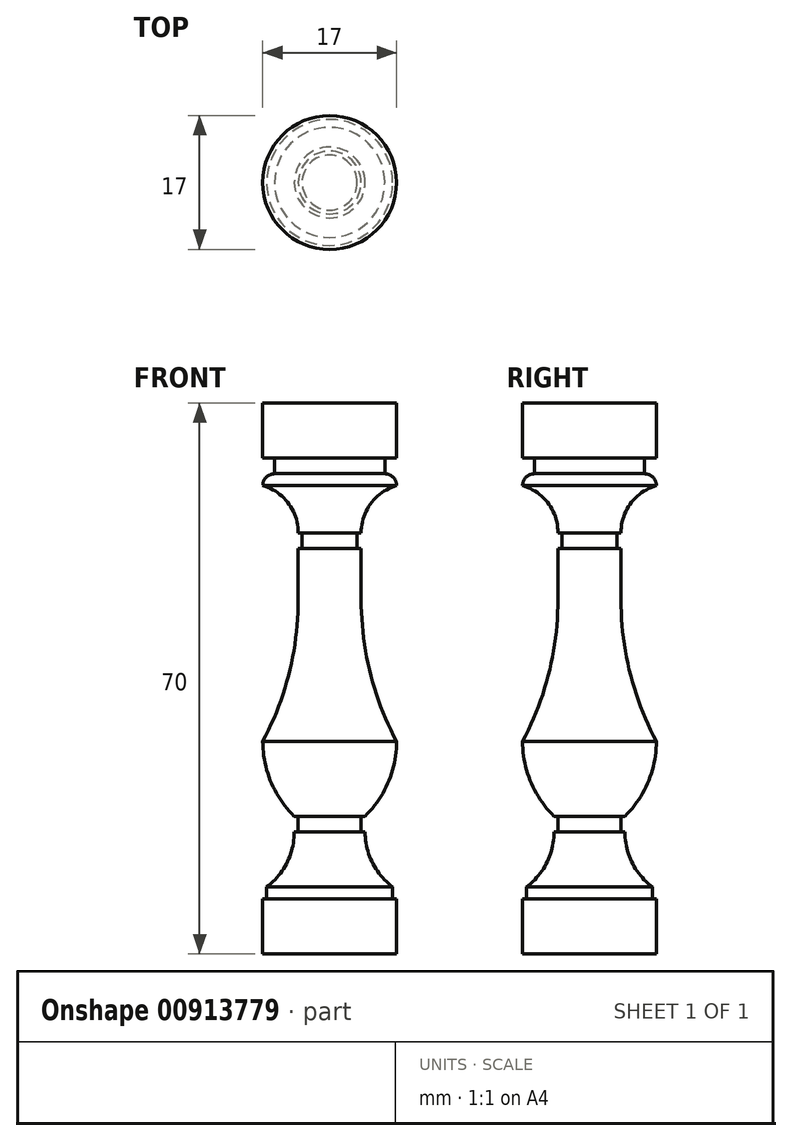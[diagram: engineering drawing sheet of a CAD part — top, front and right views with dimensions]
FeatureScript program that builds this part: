
annotation { "Feature Type Name" : "Feature", "Feature Type Description" : "" }
export const myFeature = defineFeature(function(context is Context, id is Id, definition is map)
    precondition{}
    {
        {
            var Q0;
            Q0=qCreatedBy(makeId("Front.planeOp"),FACE);
            var sketch = newSketch(context, id + "F0", { "sketchPlane" : qUnion([Q0])});
            skLineSegment(sketch, "E0", {"start": v(0, 0) * mm, "end": v(-8.5, 0) * mm});
            skLineSegment(sketch, "E1", {"start": v(-8.5, 0) * mm, "end": v(-8.5, 7) * mm});
            skLineSegment(sketch, "E2", {"start": v(-8.5, 7) * mm, "end": v(-8, 7) * mm});
            skLineSegment(sketch, "E3", {"start": v(-8, 7) * mm, "end": v(-8, 8.5) * mm});
            skArc(sketch, "E4", {"start": v(-8, 8.5) * mm, "mid": v(-5.42, 11.59) * mm, "end": v(-4.5, 15.5) * mm});
            skLineSegment(sketch, "E5", {"start": v(-4.5, 15.5) * mm, "end": v(-4, 15.5) * mm});
            skLineSegment(sketch, "E6", {"start": v(-4, 15.5) * mm, "end": v(-4, 17.5) * mm});
            skLineSegment(sketch, "E7", {"start": v(-4, 17.5) * mm, "end": v(-4.5, 17.5) * mm});
            skArc(sketch, "E8", {"start": v(-8.5, 27) * mm, "mid": v(-5.14, 35.72) * mm, "end": v(-4, 45) * mm});
            skLineSegment(sketch, "E9", {"start": v(-4, 45) * mm, "end": v(-4, 51.5) * mm});
            skLineSegment(sketch, "E10", {"start": v(-4, 51.5) * mm, "end": v(-3.5, 51.5) * mm});
            skLineSegment(sketch, "E11", {"start": v(-3.5, 51.5) * mm, "end": v(-3.5, 53.5) * mm});
            skLineSegment(sketch, "E12", {"start": v(-3.5, 53.5) * mm, "end": v(-4, 53.5) * mm});
            skArc(sketch, "E13", {"start": v(-4, 53.5) * mm, "mid": v(-5.25, 57.25) * mm, "end": v(-8.5, 59.5) * mm});
            skArc(sketch, "E14", {"start": v(-7, 61) * mm, "mid": v(-8.06, 60.56) * mm, "end": v(-8.5, 59.5) * mm});
            skLineSegment(sketch, "E15", {"start": v(-7, 61) * mm, "end": v(-7, 63) * mm});
            skLineSegment(sketch, "E16", {"start": v(-7, 63) * mm, "end": v(-8.5, 63) * mm});
            skLineSegment(sketch, "E17", {"start": v(-8.5, 63) * mm, "end": v(-8.5, 70) * mm});
            skLineSegment(sketch, "E18", {"start": v(-8.5, 70) * mm, "end": v(0, 70) * mm});
            skLineSegment(sketch, "E19", {"start": v(0, 70) * mm, "end": v(0, 0) * mm});
            skLineSegment(sketch, "E20", {"start": v(-8.5, 27) * mm, "end": v(-8.5, 32.18) * mm, "construction": true});
            skArc(sketch, "E21", {"start": v(-8.5, 27) * mm, "mid": v(-7.46, 21.85) * mm, "end": v(-4.5, 17.5) * mm});
            skSolve(sketch);
        }
        {
            var Q0;
            Q0=makeQuery(id+"F0.imprint","IMPRINT",FACE,{"disambiguationData":[TD([[makeQuery(id+"F0.imprint","IMPRINT",EDGE,{"derivedFrom":sQuery(id+"F0.wireOp",EDGE,"E0")}),-1.0]])]});
            var Q1;
            Q1=sQuery(id+"F0.wireOp",EDGE,"E19");
            revolve(context, id + "F1", {"surfaceOperationType" : NewSurfaceOperationType.NEW, "entities" : qUnion([Q0]), "axis" : qUnion([Q1]), "revolveType" : RevolveType.FULL});
        }
    });
